# Revit family: KEUCO_14964010100
name_source: partatom
category: Möbel
revit_build: Autodesk Revit 2016 (Build: 20150220_1215(x64)
units: mm (PartAtom-declared; Revit-internal decimal feet)

## family parameters
Arbeitsebenenbasiert = Nein
Beim Laden mit Abzugskörper schneiden = Nein
Gemeinsam genutzt = Nein
Immer vertikal = Ja
Raumberechnungspunkt = Nein

## types (3) — shared parameters
Beschreibung = komplett mit Kunststoff-Einsatz, Bürste mit Griff
und Ersatzbürstenkopf
Gewicht = 0.628
Hersteller = KEUCO
Kategorie = ACC
Material Abdeckung = Schwarzgrau
Preisgruppe = 1
Serie = Plan
URL = https://www.keuco.com
Verwendung = GWC / WC

## per-type parameters (varying)
| type | Ausschreibungstext | Material Bürste |
| 14964010100 | KEUCO PLAN Toilettenbürstengarnitur 14964010100
Hochglanzverchromte Toilettenbürstengarnitur 
in ästhetischem, funktionalem Design, Wandmodell
komplett mit Kunststoff-Einsatz, 
Bürste mit Griff und Ersatzbürstenkopf
herausnehmbarer Kunststoffeinsatz für leichtes Reinigen
Höhe 278 mm (Höhe inklusive Bürste 379 mm), 
Durchmesser 104 mm, Ausladung 114 mm
Die Toilettenbürstengarnitur wird verdeckt angebracht
Lieferung inkl. korrosionsfreiem Befestigungsmaterial | Verchromt |
| 14964070100 | KEUCO PLAN Toilettenbürstengarnitur 14964070100
Toilettenbürstengarnitur aus hochwertigem Edelstahl 
in ästhetischem, funktionalem Design, Wandmodell
komplett mit Kunststoff-Einsatz, 
Bürste mit Griff und Ersatzbürstenkopf
herausnehmbarer Kunststoffeinsatz für leichtes Reinigen
Höhe 278 mm (Höhe inklusive Bürste 379 mm), 
Durchmesser 104 mm, Ausladung 114 mm
Die Toilettenbürstengarnitur wird verdeckt angebracht
Lieferung inkl. korrosionsfreiem Befestigungsmaterial | Edelstahl |
| 14964170100 | KEUCO PLAN Toilettenbürstengarnitur 14964170100
Toilettenbürstengarnitur aus silber-eloxiertem Aluminium (E6 EV1) 
in ästhetischem, funktionalem Design Wandmodell, 
komplett mit Kunststoff-Einsatz, 
Bürste mit Griff und Ersatzbürstenkopf
herausnehmbarer Kunststoffeinsatz für leichtes Reinigen
Höhe 278 mm (Höhe inklusive Bürste 379 mm), 
Durchmesser 104 mm, Ausladung 114 mm
Die Toilettenbürstengarnitur wird verdeckt angebracht
Lieferung inkl. korrosionsfreiem Befestigungsmaterial | Verchromt |

note: column(s) folded — value = type name in every type: Artikelnummer

## geometry (parser evidence)
native form markers: Blend x2, Sweep x3
no freeform markers — native parametric forms only
